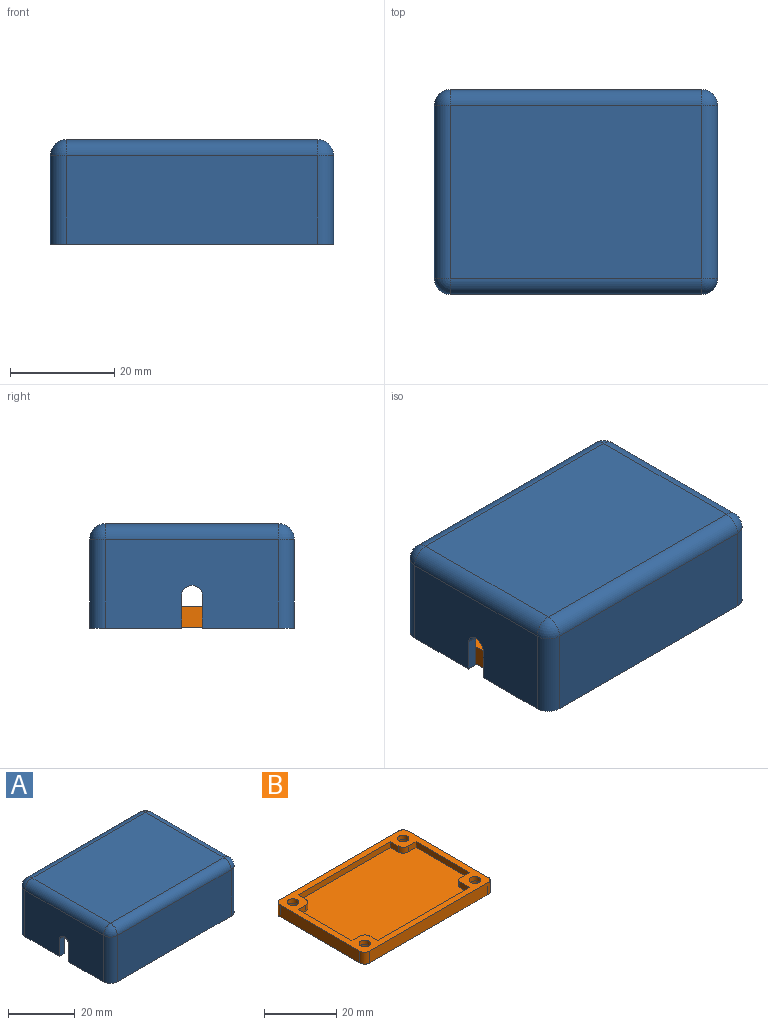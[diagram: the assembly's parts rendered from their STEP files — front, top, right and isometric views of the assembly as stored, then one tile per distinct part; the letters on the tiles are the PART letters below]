
ASSEMBLY  parts=2 mates=1
PART A: 62 faces, bbox 54.2x39.2x20 mm
  f0: plane 31.2x18mm, normal (-1,0,0), area 419.3mm2, adj f4,f8,f11,f17,f20,f22,f23,f32
  f1: plane 33.2x17mm, normal (1,0,0), area 533.3mm2, adj f4,f17,f41,f45,f47,f57,f58,f59
  f2: plane 31.2x18mm, normal (1,0,0), area 419.3mm2, adj f4,f6,f10,f17,f19,f21,f23,f34
  f3: plane 33.2x17mm, normal (-1,0,0), area 533.3mm2, adj f4,f17,f36,f38,f39,f52,f53,f54
  f4: plane 54.2x17.6mm, normal (0,0,-1), area 168.7mm2, adj f0,f1,f2,f3,f13,f15,f32,f35
  f5: plane 13.9x4mm, normal (1,0,0), area 55.6mm2, adj f13,f19,f23,f51
  f6: plane 13.9x4mm, normal (0,-1,0), area 55.6mm2, adj f2,f19,f23,f51
  f7: plane 13.9x4mm, normal (-1,0,0), area 55.6mm2, adj f13,f20,f23,f50
  f8: plane 13.9x4mm, normal (0,-1,0), area 55.6mm2, adj f0,f20,f23,f50
  f9: plane 13.9x4mm, normal (1,0,0), area 55.6mm2, adj f16,f21,f23,f49
  f10: plane 13.9x4mm, normal (0,1,0), area 55.6mm2, adj f2,f21,f23,f49
  f11: plane 13.9x4mm, normal (0,1,0), area 55.6mm2, adj f0,f22,f23,f48
  f12: plane 13.9x4mm, normal (-1,0,0), area 55.6mm2, adj f16,f22,f23,f48
  f13: plane 46.2x18mm, normal (0,-1,0), area 720.4mm2, adj f4,f5,f7,f19,f20,f23,f32,f35
  f14: plane 48.2x17mm, normal (0,-1,0), area 819.4mm2, adj f17,f38,f44,f47
  f15: plane 48.2x17mm, normal (0,1,0), area 819.4mm2, adj f4,f36,f40,f41
  f16: plane 46.2x18mm, normal (0,1,0), area 720.4mm2, adj f9,f12,f17,f21,f22,f23,f33,f34
  f17: plane 54.2x17.6mm, normal (0,0,-1), area 168.7mm2, adj f0,f1,f2,f3,f14,f16,f33,f34
  f18: plane 48.2x33.2mm, normal (0,0,1), area 1600.2mm2, adj f39,f40,f44,f45
  f19: plane 6x6mm, normal (0,0,-1), area 30.5mm2, adj f2,f5,f6,f13,f31,f35,f51
  f20: plane 6x6mm, normal (0,0,-1), area 30.5mm2, adj f0,f7,f8,f13,f29,f32,f50
  f21: plane 6x6mm, normal (0,0,-1), area 30.5mm2, adj f2,f9,f10,f16,f27,f34,f49
  f22: plane 6x6mm, normal (0,0,-1), area 30.5mm2, adj f0,f11,f12,f16,f25,f33,f48
  f23: plane 50.2x35.2mm, normal (0,0,-1), area 1626.5mm2, adj f0,f2,f5,f6,f7,f8,f9,f10
  f24: cone r=0mm half-angle=59deg, axis (0,0,-1), area 4.4mm2, adj f25
  f25: cylinder r=1.1mm len=12mm, axis (0,0,-1), area 82.9mm2, adj f22,f24
  f26: cone r=0mm half-angle=59deg, axis (0,0,-1), area 4.4mm2, adj f27
  f27: cylinder r=1.1mm len=12mm, axis (0,0,-1), area 82.9mm2, adj f21,f26
  f28: cone r=0mm half-angle=59deg, axis (0,0,-1), area 4.4mm2, adj f29
  f29: cylinder r=1.1mm len=12mm, axis (0,0,-1), area 82.9mm2, adj f20,f28
  f30: cone r=0mm half-angle=59deg, axis (0,0,-1), area 4.4mm2, adj f31
  f31: cylinder r=1.1mm len=12mm, axis (0,0,-1), area 82.9mm2, adj f19,f30
  f32: cylinder r=2mm len=4.1mm, axis (0,0,-1), area 12.9mm2, adj f0,f4,f13,f20
  f33: cylinder r=2mm len=4.1mm, axis (0,0,1), area 12.9mm2, adj f0,f16,f17,f22
  f34: cylinder r=2mm len=4.1mm, axis (0,0,-1), area 12.9mm2, adj f2,f16,f17,f21
  f35: cylinder r=2mm len=4.1mm, axis (0,0,1), area 12.9mm2, adj f2,f4,f13,f19
  f36: cylinder r=3mm len=17mm, axis (0,0,-1), area 80.1mm2, adj f3,f4,f15,f37
  f37: sphere r=3mm, area 14.1mm2, adj f36,f39,f40
  f38: cylinder r=3mm len=17mm, axis (0,0,1), area 80.1mm2, adj f3,f14,f17,f42
  f39: cylinder r=3mm len=33.2mm, axis (0,-1,0), area 156.5mm2, adj f3,f18,f37,f42
  f40: cylinder r=3mm len=48.2mm, axis (-1,0,0), area 227.1mm2, adj f15,f18,f37,f43
  f41: cylinder r=3mm len=17mm, axis (0,0,1), area 80.1mm2, adj f1,f4,f15,f43
  f42: sphere r=3mm, area 14.1mm2, adj f38,f39,f44
  f43: sphere r=3mm, area 14.1mm2, adj f40,f41,f45
  f44: cylinder r=3mm len=48.2mm, axis (1,0,0), area 227.1mm2, adj f14,f18,f42,f46
  f45: cylinder r=3mm len=33.2mm, axis (0,1,0), area 156.5mm2, adj f1,f18,f43,f46
  f46: sphere r=3mm, area 14.1mm2, adj f44,f45,f47
  f47: cylinder r=3mm len=17mm, axis (0,0,-1), area 80.1mm2, adj f1,f14,f17,f46
  f48: cylinder r=2mm len=13.9mm, axis (0,0,1), area 43.7mm2, adj f11,f12,f22,f23
  f49: cylinder r=2mm len=13.9mm, axis (0,0,1), area 43.7mm2, adj f9,f10,f21,f23
  f50: cylinder r=2mm len=13.9mm, axis (0,0,1), area 43.7mm2, adj f7,f8,f20,f23
  f51: cylinder r=2mm len=13.9mm, axis (0,0,1), area 43.7mm2, adj f5,f6,f19,f23
  f52: plane 6.29x2mm, normal (0,1,0), area 12.6mm2, adj f2,f3,f17,f53
  f53: cylinder r=2mm len=2mm, axis (1,0,0), area 6.1mm2, adj f2,f3,f52,f54
  f54: plane 2x0mm, normal (0,0,-1), area 0mm2, adj f2,f3,f53,f55
  f55: cylinder r=2mm len=2mm, axis (1,0,0), area 6.1mm2, adj f2,f3,f54,f56
  f56: plane 6.31x2mm, normal (0,-1,0), area 12.6mm2, adj f2,f3,f4,f55
  f57: cylinder r=2mm len=2mm, axis (1,0,0), area 6.1mm2, adj f0,f1,f58,f60
  f58: plane 2x0mm, normal (0,0,-1), area 0mm2, adj f0,f1,f57,f59
  f59: cylinder r=2mm len=2mm, axis (1,0,0), area 6.1mm2, adj f0,f1,f58,f61
  f60: plane 6.31x2mm, normal (0,-1,0), area 12.6mm2, adj f0,f1,f4,f57
  f61: plane 6.29x2mm, normal (0,1,0), area 12.6mm2, adj f0,f1,f17,f59
PART B: 39 faces, bbox 50x35x4 mm
  f0: cylinder r=1.6mm len=3.2mm, axis (0,0,-1), area 14.7mm2, adj f20,f32
  f1: cylinder r=1.6mm len=3.2mm, axis (0,0,-1), area 14.7mm2, adj f20,f28
  f2: cylinder r=1.6mm len=3.2mm, axis (0,0,-1), area 14.7mm2, adj f20,f34
  f3: cylinder r=1.6mm len=3.2mm, axis (0,0,-1), area 14.7mm2, adj f20,f30
  f4: plane 21x2mm, normal (1,0,0), area 42mm2, adj f13,f14,f20,f22
  f5: plane 36x2mm, normal (0,-1,0), area 72mm2, adj f15,f16,f20,f22
  f6: plane 21x2mm, normal (-1,0,0), area 42mm2, adj f17,f18,f20,f22
  f7: plane 46.2x4mm, normal (0,-1,0), area 184.8mm2, adj f20,f21,f23,f26
  f8: plane 31.2x4mm, normal (1,0,0), area 124.8mm2, adj f20,f21,f23,f24
  f9: plane 46.2x4mm, normal (0,1,0), area 184.8mm2, adj f20,f21,f24,f25
  f10: plane 4x2mm, normal (-1,0,0), area 8mm2, adj f11,f20,f22,f27
  f11: plane 36x2mm, normal (0,1,0), area 72mm2, adj f10,f12,f20,f22
  f12: plane 3x2mm, normal (1,0,0), area 6mm2, adj f11,f20,f22,f36
  f13: plane 3x2mm, normal (0,1,0), area 6mm2, adj f4,f20,f22,f36
  f14: plane 3x2mm, normal (0,-1,0), area 6mm2, adj f4,f20,f22,f37
  f15: plane 3x2mm, normal (1,0,0), area 6mm2, adj f5,f20,f22,f37
  f16: plane 3x2mm, normal (-1,0,0), area 6mm2, adj f5,f20,f22,f38
  f17: plane 3x2mm, normal (0,-1,0), area 6mm2, adj f6,f20,f22,f38
  f18: plane 4x2mm, normal (0,1,0), area 8mm2, adj f6,f20,f22,f27
  f19: plane 31.2x4mm, normal (-1,0,0), area 124.8mm2, adj f20,f21,f25,f26
  f20: plane 50x35mm, normal (0,0,1), area 385.9mm2, adj f0,f1,f2,f3,f4,f5,f6,f7
  f21: plane 50x35mm, normal (0,0,-1), area 1668.4mm2, adj f7,f8,f9,f19,f23,f24,f25,f26
  f22: plane 46x31mm, normal (0,0,1), area 1328.8mm2, adj f4,f5,f6,f10,f11,f12,f13,f14
  f23: cylinder r=1.9mm len=4mm, axis (0,0,1), area 11.9mm2, adj f7,f8,f20,f21
  f24: cylinder r=1.9mm len=4mm, axis (0,0,-1), area 11.9mm2, adj f8,f9,f20,f21
  f25: cylinder r=1.9mm len=4mm, axis (0,0,1), area 11.9mm2, adj f9,f19,f20,f21
  f26: cylinder r=1.9mm len=4mm, axis (0,0,-1), area 11.9mm2, adj f7,f19,f20,f21
  f27: cylinder r=1mm len=2mm, axis (0,0,-1), area 3.1mm2, adj f10,f18,f20,f22
  f28: cone r=0mm half-angle=59deg, axis (0,0,-1), area 13.5mm2, adj f1,f29
  f29: cylinder r=2.5mm len=5mm, axis (0,0,-1), area 31.4mm2, adj f21,f28
  f30: cone r=0mm half-angle=59deg, axis (0,0,-1), area 13.5mm2, adj f3,f31
  f31: cylinder r=2.5mm len=5mm, axis (0,0,-1), area 31.4mm2, adj f21,f30
  f32: cone r=0mm half-angle=59deg, axis (0,0,-1), area 13.5mm2, adj f0,f33
  f33: cylinder r=2.5mm len=5mm, axis (0,0,-1), area 31.4mm2, adj f21,f32
  f34: cone r=0mm half-angle=59deg, axis (0,0,-1), area 13.5mm2, adj f2,f35
  f35: cylinder r=2.5mm len=5mm, axis (0,0,-1), area 31.4mm2, adj f21,f34
  f36: cylinder r=2mm len=2mm, axis (0,0,-1), area 6.3mm2, adj f12,f13,f20,f22
  f37: cylinder r=2mm len=2mm, axis (0,0,-1), area 6.3mm2, adj f14,f15,f20,f22
  f38: cylinder r=2mm len=2mm, axis (0,0,-1), area 6.3mm2, adj f16,f17,f20,f22
PLACE A t=(-2.05,1.55,0)mm
PLACE B t=(-2.05,51.55,-19.9)mm
MATE slider B.f2 <-> A.f30  axis (0,0,-1) through (-23.55,15.55,-15.9)mm
